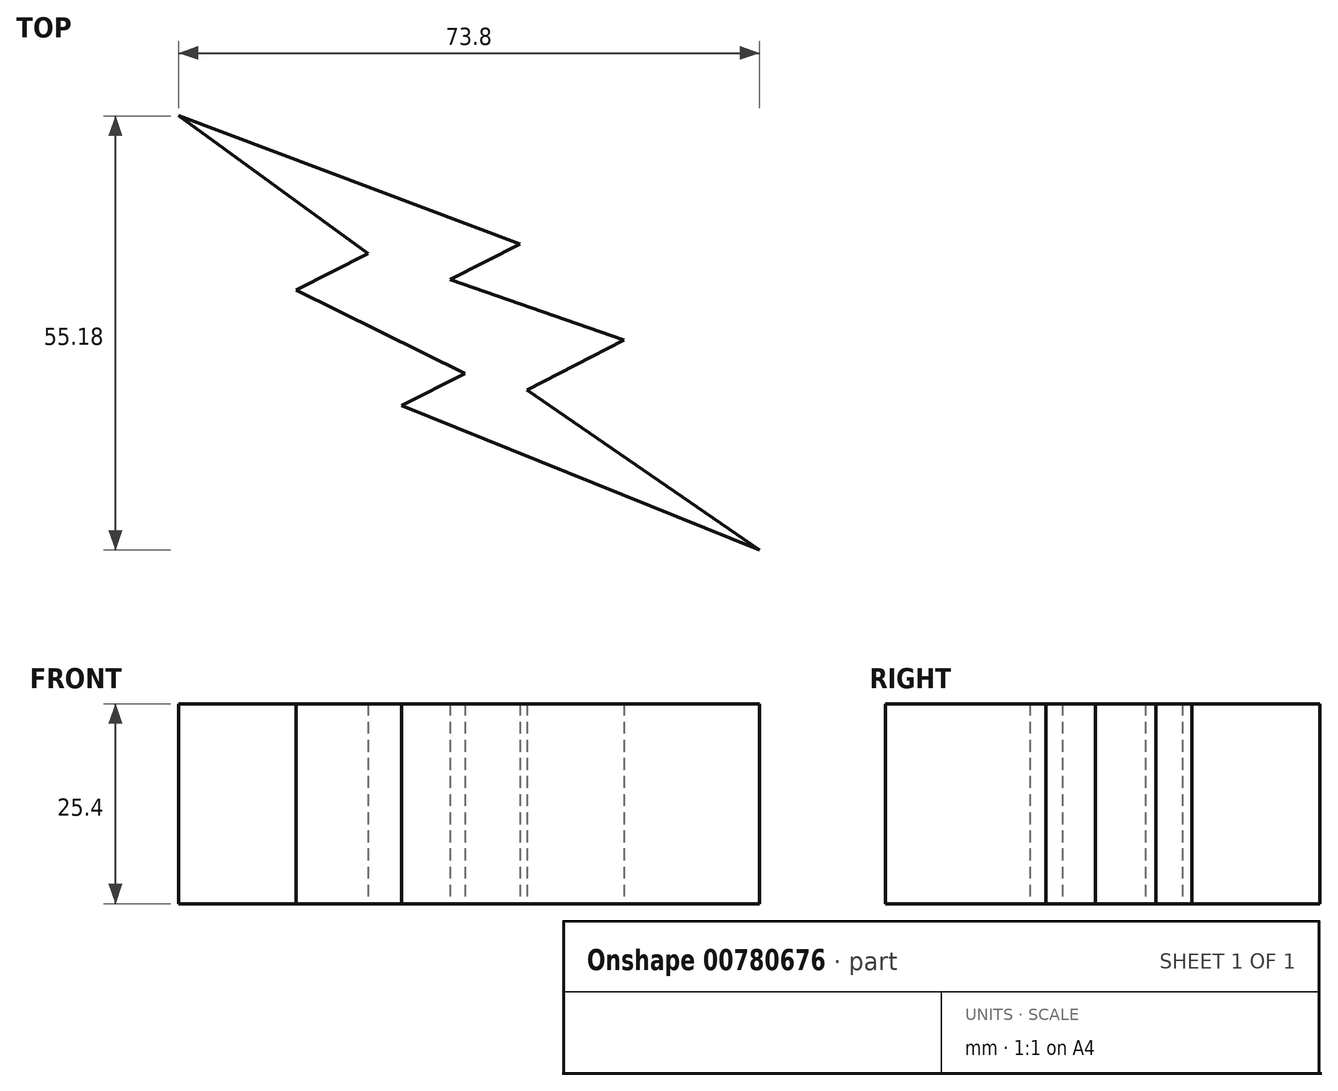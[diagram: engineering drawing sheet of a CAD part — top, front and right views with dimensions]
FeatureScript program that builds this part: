
annotation { "Feature Type Name" : "Feature", "Feature Type Description" : "" }
export const myFeature = defineFeature(function(context is Context, id is Id, definition is map)
    precondition{}
    {
        {
            var Q0;
            Q0=qCreatedBy(makeId("Top.planeOp"),FACE);
            var sketch = newSketch(context, id + "F0", { "sketchPlane" : qUnion([Q0])});
            skLineSegment(sketch, "E0.MirrorCS", {"start": v(-11.2, 10.15) * mm, "end": v(-35.26, 27.63) * mm});
            skLineSegment(sketch, "E1.MirrorCS", {"start": v(-35.26, 27.63) * mm, "end": v(8.12, 11.37) * mm});
            skLineSegment(sketch, "E2.MirrorCS", {"start": v(1.13, -5.07) * mm, "end": v(-20.32, 5.5) * mm});
            skLineSegment(sketch, "E3.MirrorCS", {"start": v(-20.32, 5.5) * mm, "end": v(-11.2, 10.15) * mm});
            skLineSegment(sketch, "E4.MirrorCS", {"start": v(8.12, 11.37) * mm, "end": v(-0.75, 6.84) * mm});
            skLineSegment(sketch, "E5.MirrorCS", {"start": v(-0.75, 6.84) * mm, "end": v(21.34, -0.88) * mm});
            skLineSegment(sketch, "E6.MirrorCS", {"start": v(21.34, -0.88) * mm, "end": v(9, -7.18) * mm});
            skLineSegment(sketch, "E7.MirrorCS", {"start": v(9, -7.18) * mm, "end": v(38.54, -27.55) * mm});
            skLineSegment(sketch, "E8.MirrorCS", {"start": v(38.54, -27.55) * mm, "end": v(-6.91, -9.18) * mm});
            skLineSegment(sketch, "E9.MirrorCS", {"start": v(-6.91, -9.18) * mm, "end": v(1.13, -5.07) * mm});
            skSolve(sketch);
        }
        {
            var Q0;
            Q0=makeQuery(id+"F0.imprint","IMPRINT",FACE,{"disambiguationData":[TD([[makeQuery(id+"F0.imprint","IMPRINT",EDGE,{"derivedFrom":sQuery(id+"F0.wireOp",EDGE,"E0.MirrorCS")}),-1.0]])]});
            extrude(context, id + "F1", {"entities" : qUnion([Q0]), "depth" : 25.4 * mm, "offsetDistance" : 25.4 * mm});
        }
    });
